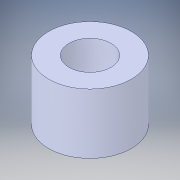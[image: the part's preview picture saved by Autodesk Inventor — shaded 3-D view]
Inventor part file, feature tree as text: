
AUTODESK INVENTOR PART (.ipt)
format: ipt  version: 2018 (Build 220112000, 112)  size: 104,448 bytes
history: native  units: in
note: dims shown in document units (in); Inventor stores cm internally (conversion verified against a paired STEP export)
features: extrude x1, sketch x1, other x1
ambient origin geometry x8: Origin, YZ Plane, XZ Plane, XY Plane, X Axis, Y Axis, Z Axis, Center Point
bodies: Solid1 (feature_tree)
feature tree (3):
  extrude  "Extrusion1"  [1 undecoded]
  sketch  "Sketch1"  dims[d0=0.305in d1=0.0in]
  other  "Boss-Extrude1"
note: 1 required parameter value undecoded (feature->parameter linkage not recoverable at this tier; creation-order binding heuristic only, values carry confidence <= 0.55)
